# Revit family: Hekatron_Feststellanlagen_Gasmesscomputer 8022 230V_DE_22.01
name_source: partatom
category: Brandmelder
revit_build: Autodesk Revit 2018 (Build: 20190510_1515(x64)
units: mm (PartAtom-declared; Revit-internal decimal feet)

## family parameters
Basisbauteil = Fläche
Beim Laden mit Abzugskörper schneiden = Nein
Bemaßung runder Anschluss = Durchmesser verwenden
Beschriftungsausrichtung beibehalten = Ja
Gemeinsam genutzt = Nein
OmniClass-Nummer = 23.85.30.21
OmniClass-Titel = Environmental Detection/Registration
Raumberechnungspunkt = Nein
Teiletyp = Normal

## types (1)
- Gas measuring computer 8022 230V
    Beschreibung = Gasmesscomputer, eingebaut in einem Gehäuse mit integriertem Netzteil und vorverdrahteten Anschlussklemmen. Es können bis zu zwei Messfühler für explosionsfähige Dämpfe und Gase angeschlossen werden.
    Betriebsspannung = 230 V AC
    Breite (mm) = 142.0
    Farbe = grau
    Hersteller = Hekatron
    Höhe (mm) = 450.0
    Kabeleinführung = unten
    Link zu Ausschreibungstext = https://www.meinhplus.de
    Link zu Produktinformation = https://www.hekatron-planungstools.de
    Link zu ausschreiben.de = http://www.ausschreiben.de
    Material = Kunststoff
    Modell = Gasmesscomputer 8022 230V
    Montageart = Aufputz
    Schutzart = IP 54
    Stromaufnahme = 110mA
    Tiefe (mm) = 300.0
    Typenkommentare = Gasmesscomputer
    UB A&S Artikel Nummer = 6900333
    URL = https://www.hekatron-brandschutz.de
    Version des BIM Objektes = 22.01
    Vorgabe-Ansicht = 1200 mm
    Zulässige Umgebungstemperatur = 0 °C bis +55 °C

## geometry (parser evidence)
native form markers: Sweep x2
no freeform markers — native parametric forms only
